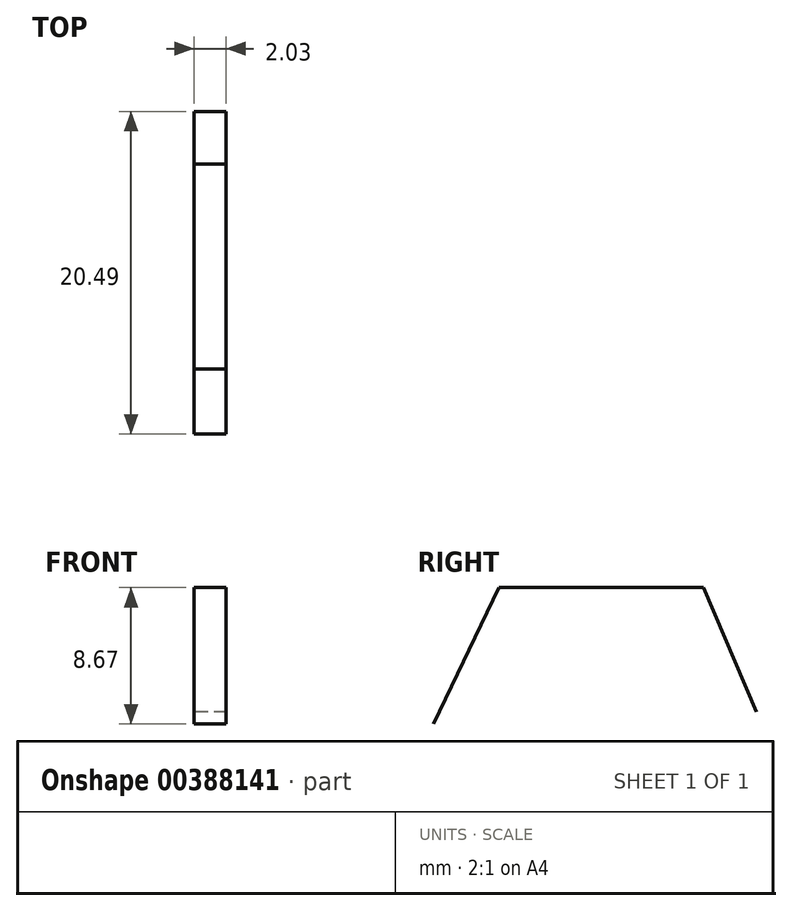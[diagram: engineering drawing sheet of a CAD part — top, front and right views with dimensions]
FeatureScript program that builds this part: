
annotation { "Feature Type Name" : "Feature", "Feature Type Description" : "" }
export const myFeature = defineFeature(function(context is Context, id is Id, definition is map)
    precondition{}
    {
        {
            var Q0;
            Q0=qCreatedBy(makeId("Right.planeOp"),FACE);
            var sketch = newSketch(context, id + "F0", { "sketchPlane" : qUnion([Q0])});
            skLineSegment(sketch, "E0", {"start": v(-28.18, -34.68) * mm, "end": v(-24.04, -26.01) * mm});
            skLineSegment(sketch, "E1", {"start": v(-24.04, -26.01) * mm, "end": v(-11.04, -26.01) * mm});
            skLineSegment(sketch, "E2", {"start": v(-11.04, -26.01) * mm, "end": v(-7.69, -33.9) * mm});
            skSolve(sketch);
        }
        {
            var Q0;
            Q0=sQuery(id+"F0.wireOp",EDGE,"E0");
            var Q1;
            Q1=sQuery(id+"F0.wireOp",EDGE,"E1");
            var Q2;
            Q2=sQuery(id+"F0.wireOp",EDGE,"E2");
            extrude(context, id + "F1", {"bodyType" : ToolBodyType.SURFACE, "surfaceEntities" : qUnion([Q0, Q1, Q2]), "oppositeDirection" : true, "depth" : 2.03 * mm});
        }
    });
